# Revit family: Herz Strömax 4215 W IG-AG
name_source: partatom
category: Rohrzubehör
units: mm (PartAtom-declared; Revit-internal decimal feet)

## family parameters
Arbeitsebenenbasiert = Nein
Beim Laden mit Abzugskörper schneiden = Nein
Bemaßung runder Anschluss = Durchmesser verwenden
Gemeinsam genutzt = Nein
Immer vertikal = Ja
OmniClass-Nummer = 23.65.55.14
OmniClass-Titel = Valves for Liquid Services
Teiletyp = Unterbricht

## types (1)
- Herz Strömax 4215 W IG-AG
    Application = For shutting off drinking water pipes and systems in buildings.
    Body = DZR brass acc. to EN1982
    H01 = 26 mm  [stored 0.0853018 ft]
    H02 = 5 mm  [stored 0.0164042 ft]
    H03 = 15 mm  [stored 0.0492126 ft]
    H04 = 21 mm  [stored 0.0688976 ft]
    Hand wheel = plastic, green
    Hersteller = HERZ Armaturen Ges.m.b.H
    L00 = 30 mm  [stored 0.0984252 ft]
    L01 = 13 mm
    L02 = 12 mm  [stored 0.0393701 ft]
    L03 = 17 mm  [stored 0.0557743 ft]
    L04 = 38 mm  [stored 0.124672 ft]
    L05 = 9 mm
    L06 = 18 mm  [stored 0.0590551 ft]
    Max. differential pressure on closed seat = 1000000.0 Pa
    Max. operating pressure = 1000000.0 Pa
    Max. operating temperature = 90 °C
    Medium = Water
    Note = Pursuant to Article 33 of the REACH Regulation (EC No. 1907/2006), we are obliged to point out that the material lead is listed on the SVHC list and that all brass components manufactured in our products exceed 0.1% (w / w) lead (CAS: 7439-92-1 / EINECS: 231-100-4).
Since lead is a component part of an alloy, actual exposure is not possible and therefore no additional information on safe use is necessary.
    O-Rings = EPDM
    Part number = 2412561
    R01 = 16 mm  [stored 0.0524934 ft]
    R03 = 15 mm  [stored 0.0492126 ft]
    R07 = 3 mm  [stored 0.00984252 ft]
    S03 = 60 mm  [stored 0.19685 ft]
    SCTWCODE = 04;01;02
    SCTWSEQ = FW;SBT_TYP_FW="106";2
    SC_NennweiteBerechnet = 0
    T01 = 18 mm  [stored 0.0590551 ft]
    URL = www.herzvalves.com
    Vorgabe-Ansicht = 0 mm  [stored 0 ft]

note: [stored X ft] marks values corroborated as IEEE doubles in the binary element streams (Revit-internal decimal feet)
